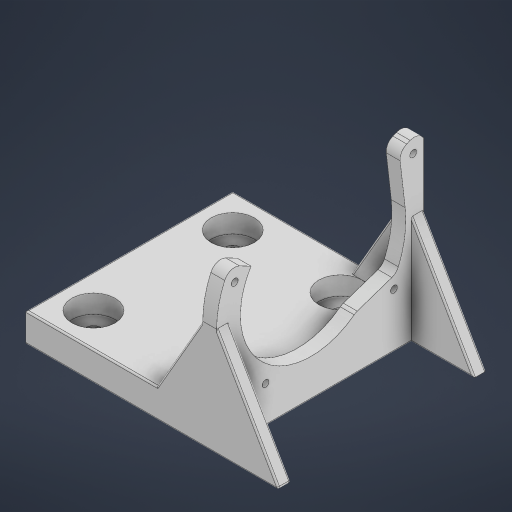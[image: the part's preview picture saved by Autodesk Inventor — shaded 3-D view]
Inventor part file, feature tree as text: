
AUTODESK INVENTOR PART (.ipt)
format: ipt  version: 2024.2 (Build 282272000, 272)  size: 434,688 bytes
history: native  units: mm
features: extrude x8, projected_geometry x7, sketch x6, fillet x6
ambient origin geometry x8: Origin, YZ Plane, XZ Plane, XY Plane, X Axis, Y Axis, Z Axis, Center Point
bodies: Solid1 (feature_tree)
feature tree (27):
  sketch  "Sketch1"  dims[d0=92.0mm d1=4.5mm d2=4.5mm d3=4.5mm]
  extrude  "Extrusion1"  Depth=4.5mm
  fillet  "Fillet2"  Radius=4.5mm
  fillet  "Fillet3"  Radius=4.5mm
  extrude  "Extrusion2"  Depth=9.0mm TaperAngle=0.0deg
  fillet  "Fillet4"  Radius=29.632551mm
  sketch  "Sketch3"  dims[d4=4.5mm d19=9.0mm d20=0.0mm d28=29.632551mm]
  extrude  "Extrusion3"  Depth=49.730102mm
  extrude  "Extrusion4"  Depth=20.6185mm
  extrude  "Extrusion5"  Depth=35.077154mm
  extrude  "Extrusion6"  Depth=7.0mm
  extrude  "Extrusion7"  TaperAngle=90.0deg  [1 undecoded]
  fillet  "Fillet5"  [1 undecoded]
  fillet  "Fillet6"  Radius=4.0mm
  extrude  "Extrusion8"  Depth=1.0mm
  fillet  "Fillet7"  Radius=115.0mm
  projected_geometry  "Projected Loop2"
  sketch  "Sketch4"  dims[d29=53.762531mm d30=49.730102mm]
  projected_geometry  "Projected Loop3"
  sketch  "Sketch5"  dims[d31=66.269898mm d32=20.6185mm]
  projected_geometry  "Projected Loop4"
  projected_geometry  "Projected Loop5"
  sketch  "Sketch6"  dims[d33=46.434378mm d34=35.077154mm]
  projected_geometry  "Projected Loop6"
  sketch  "Sketch7"  dims[d35=34.971475mm d36=7.0mm d37=90.0deg d38=180.0deg d39=4.0mm d40=1.0mm d41=115.0mm d42=0.0mm d43=1.0mm d44=28.0mm d45=10.0mm d46=28.0mm d47=10.0mm d48=28.0mm d49=10.0mm d50=28.0mm d51=10.0mm d52=134.463844mm d53=124.0mm d54=22.0mm d55=45.231922mm d56=22.0mm d57=45.231922mm d58=90.463844mm d59=32.0mm d60=32.0mm d61=22.0mm d62=22.0mm d63=22.0mm d64=22.0mm d65=12.0mm d66=0.0mm d67=20.0mm d68=123.0mm d69=0.0mm d70=120.0deg d71=8.0mm d72=0.0mm d73=8.0mm d74=0.0mm d75=60.0deg d76=8.0mm d77=0.0mm d78=1.0mm d79=1.0mm d80=8.0mm d81=0.0mm d82=1.0mm]
  projected_geometry  "Projected Loop7"
  projected_geometry  "Projected Loop8"
note: 2 required parameter values undecoded (feature->parameter linkage not recoverable at this tier; creation-order binding heuristic only, values carry confidence <= 0.55)
